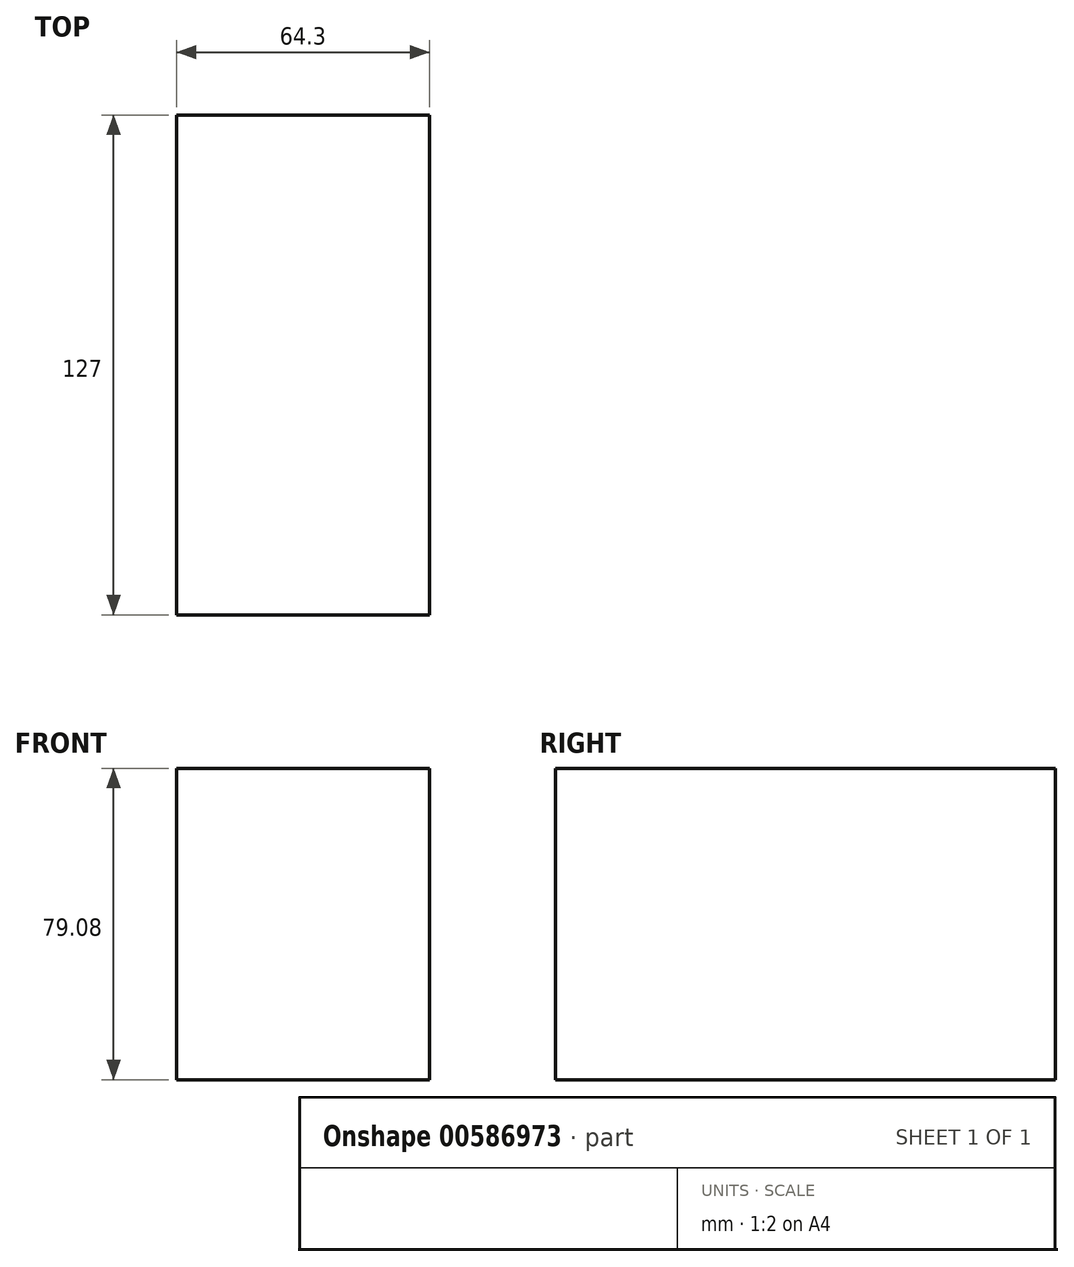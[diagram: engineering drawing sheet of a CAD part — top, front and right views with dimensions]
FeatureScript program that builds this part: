
annotation { "Feature Type Name" : "Feature", "Feature Type Description" : "" }
export const myFeature = defineFeature(function(context is Context, id is Id, definition is map)
    precondition{}
    {
        {
            var Q0;
            Q0=qCreatedBy(makeId("Front.planeOp"),FACE);
            var sketch = newSketch(context, id + "F0", { "sketchPlane" : qUnion([Q0])});
            skLineSegment(sketch, "E0", {"start": v(0, 79.08) * mm, "end": v(64.3, 79.08) * mm});
            skLineSegment(sketch, "E1", {"start": v(64.3, 79.08) * mm, "end": v(64.3, 0) * mm});
            skLineSegment(sketch, "E2", {"start": v(64.3, 0) * mm, "end": v(0, 0) * mm});
            skLineSegment(sketch, "E3", {"start": v(0, 0) * mm, "end": v(0, 79.08) * mm});
            skSolve(sketch);
        }
        {
            var Q0;
            Q0=makeQuery(id+"F0.imprint","IMPRINT",FACE,{"disambiguationData":[TD([[makeQuery(id+"F0.imprint","IMPRINT",EDGE,{"derivedFrom":sQuery(id+"F0.wireOp",EDGE,"E0")}),-1.0]])]});
            extrude(context, id + "F1", {"entities" : qUnion([Q0]), "depth" : 127 * mm, "offsetDistance" : 25.4 * mm});
        }
    });
